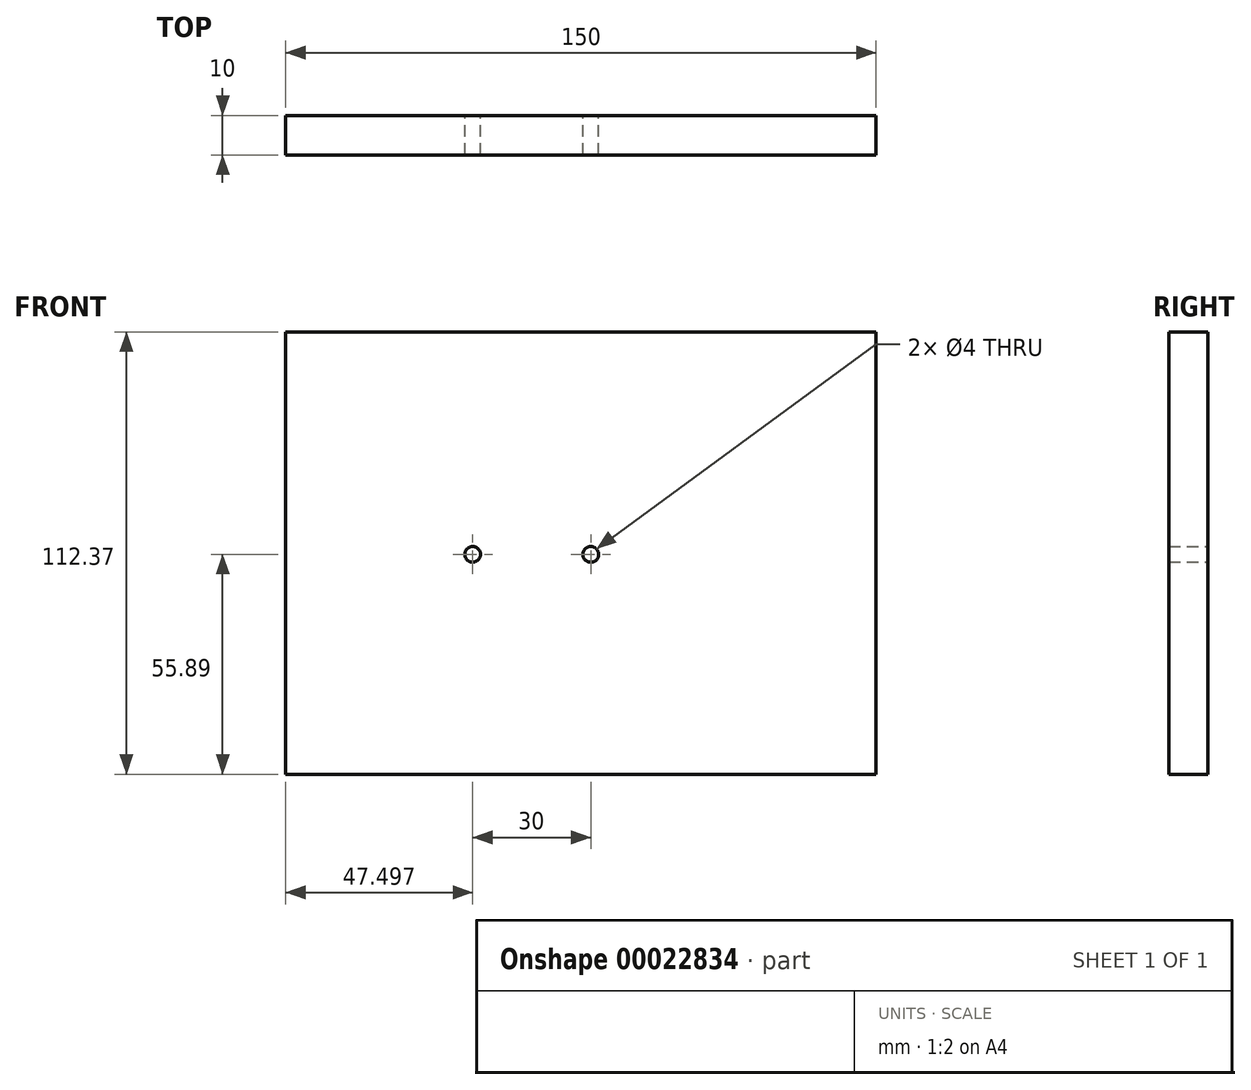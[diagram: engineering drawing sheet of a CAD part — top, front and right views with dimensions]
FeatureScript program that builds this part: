
annotation { "Feature Type Name" : "Feature", "Feature Type Description" : "" }
export const myFeature = defineFeature(function(context is Context, id is Id, definition is map)
    precondition{}
    {
        {
            var Q0;
            Q0=qCreatedBy(makeId("Front.planeOp"),FACE);
            var sketch = newSketch(context, id + "F0", { "sketchPlane" : qUnion([Q0])});
            skLineSegment(sketch, "E0.bottom", {"start": v(-99.85, 56.48) * mm, "end": v(50.15, 56.48) * mm});
            skLineSegment(sketch, "E0.top", {"start": v(-99.85, -55.9) * mm, "end": v(50.15, -55.9) * mm});
            skLineSegment(sketch, "E0.left", {"start": v(-99.85, 56.48) * mm, "end": v(-99.85, -55.9) * mm});
            skLineSegment(sketch, "E0.right", {"start": v(50.15, 56.48) * mm, "end": v(50.15, -55.9) * mm});
            skCircle(sketch, "E1", {"center": v(-52.35, 0) * mm, "radius": 2 * mm});
            skCircle(sketch, "E2", {"center": v(-22.35, 0) * mm, "radius": 2 * mm});
            skLineSegment(sketch, "E3", {"start": v(-52.35, 0) * mm, "end": v(-22.35, 0) * mm});
            skSolve(sketch);
        }
        {
            var Q0;
            Q0=makeQuery(id+"F0.imprint","IMPRINT",FACE,{"disambiguationData":[TD([[makeQuery(id+"F0.imprint","IMPRINT",EDGE,{"derivedFrom":sQuery(id+"F0.wireOp",EDGE,"E0.bottom")}),-1.0]])]});
            extrude(context, id + "F1", {"entities" : qUnion([Q0]), "depth" : 10 * mm});
        }
    });
